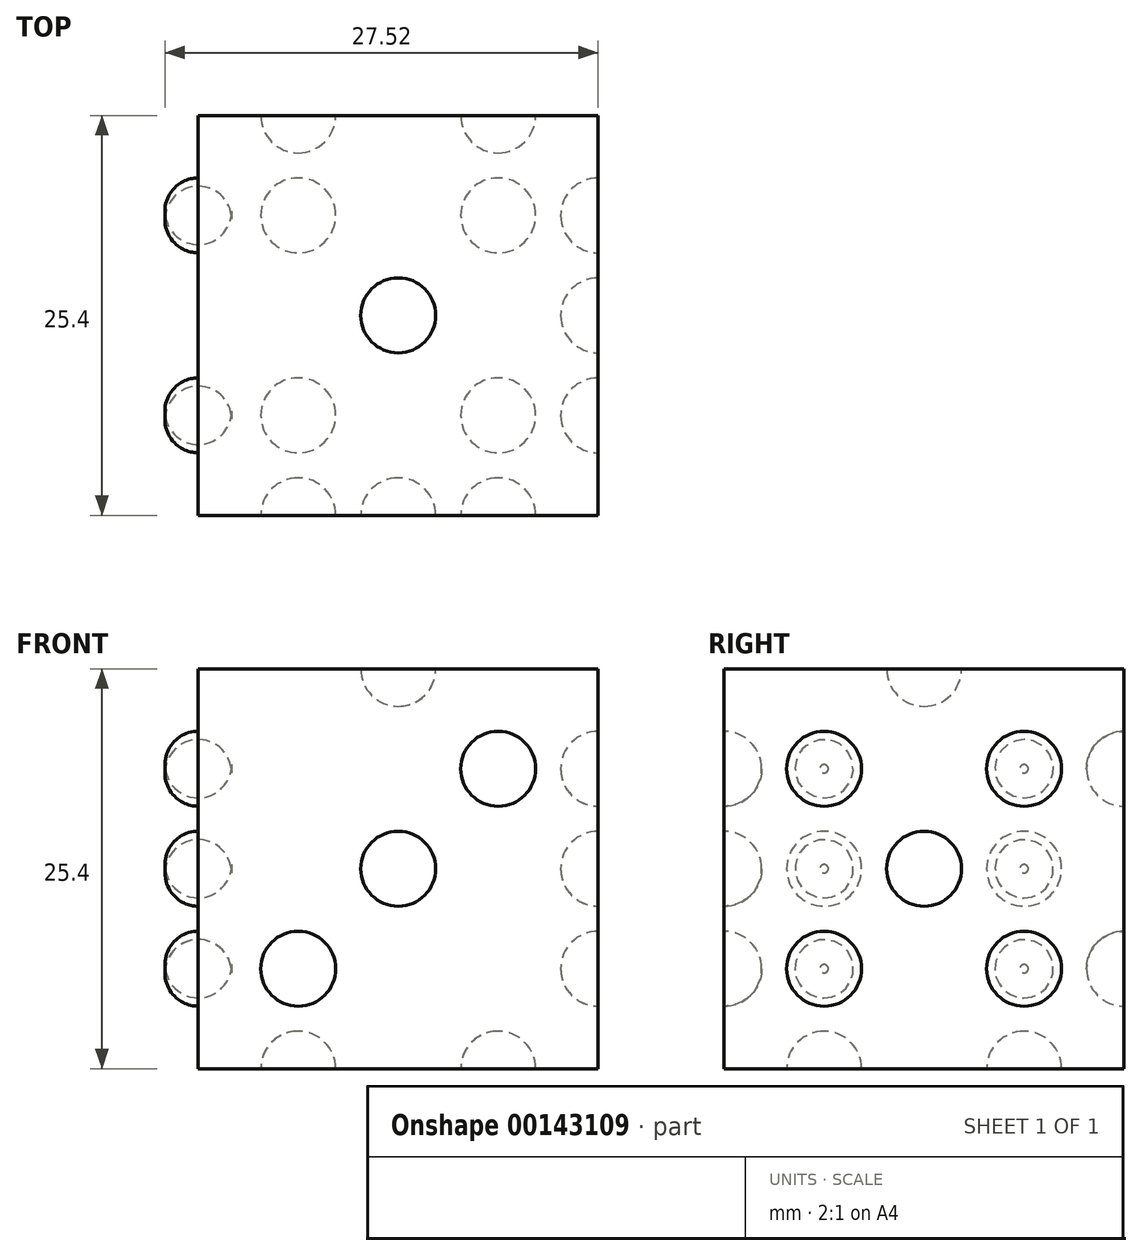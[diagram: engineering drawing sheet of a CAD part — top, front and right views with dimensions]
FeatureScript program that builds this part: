
annotation { "Feature Type Name" : "Feature", "Feature Type Description" : "" }
export const myFeature = defineFeature(function(context is Context, id is Id, definition is map)
    precondition{}
    {
        {
            var Q0;
            Q0=qCreatedBy(makeId("Front.planeOp"),FACE);
            var sketch = newSketch(context, id + "F0", { "sketchPlane" : qUnion([Q0])});
            skLineSegment(sketch, "E0.bottom", {"start": v(0, 0) * mm, "end": v(25.4, 0) * mm});
            skLineSegment(sketch, "E0.top", {"start": v(0, 25.4) * mm, "end": v(25.4, 25.4) * mm});
            skLineSegment(sketch, "E0.left", {"start": v(0, 0) * mm, "end": v(0, 25.4) * mm});
            skLineSegment(sketch, "E0.right", {"start": v(25.4, 0) * mm, "end": v(25.4, 25.4) * mm});
            skSolve(sketch);
        }
        {
            var Q0;
            Q0=makeQuery(id+"F0.imprint","IMPRINT",FACE,{"disambiguationData":[TD([[makeQuery(id+"F0.imprint","IMPRINT",EDGE,{"derivedFrom":sQuery(id+"F0.wireOp",EDGE,"E0.bottom")}),1.0]])]});
            extrude(context, id + "F1", {"entities" : qUnion([Q0]), "oppositeDirection" : true, "depth" : 25.4 * mm});
        }
        {
            var Q0;
            Q0=makeQuery(id+"F1.opExtrude","CAP_FACE",FACE,{"disambiguationData":[OSD([sQuery(id+"F0.wireOp",EDGE,"E0.bottom"),sQuery(id+"F0.wireOp",EDGE,"E0.top"),sQuery(id+"F0.wireOp",EDGE,"E0.left"),sQuery(id+"F0.wireOp",EDGE,"E0.right")])],"isStart":true});
            var sketch = newSketch(context, id + "F2", { "sketchPlane" : qUnion([Q0])});
            skCircle(sketch, "E1", {"center": v(6.35, 6.35) * mm, "radius": 2.38 * mm});
            skCircle(sketch, "E2", {"center": v(12.7, 12.7) * mm, "radius": 2.38 * mm});
            skCircle(sketch, "E3", {"center": v(19.05, 19.05) * mm, "radius": 2.38 * mm});
            skSolve(sketch);
        }
        {
            var Q0;
            Q0=makeQuery(id+"F2.imprint","IMPRINT",FACE,{"disambiguationData":[TD([[makeQuery(id+"F2.imprint","IMPRINT",EDGE,{"derivedFrom":sQuery(id+"F2.wireOp",EDGE,"E1")}),1.0]])]});
            var Q1;
            Q1=makeQuery(id+"F2.imprint","IMPRINT",FACE,{"disambiguationData":[TD([[makeQuery(id+"F2.imprint","IMPRINT",EDGE,{"derivedFrom":sQuery(id+"F2.wireOp",EDGE,"E2")}),1.0]])]});
            var Q2;
            Q2=makeQuery(id+"F2.imprint","IMPRINT",FACE,{"disambiguationData":[TD([[makeQuery(id+"F2.imprint","IMPRINT",EDGE,{"derivedFrom":sQuery(id+"F2.wireOp",EDGE,"E3")}),1.0]])]});
            extrude(context, id + "F3", {"entities" : qUnion([Q0, Q1, Q2]), "operationType" : NewBodyOperationType.REMOVE, "oppositeDirection" : true, "depth" : 2.38 * mm});
        }
        {
            var Q0;
            Q0=makeQuery(id+"F3.boolean.opBoolean","COPY",FACE,{"derivedFrom":makeQuery(id+"F3.opExtrude","CAP_FACE",FACE,{"disambiguationData":[OSD([sQuery(id+"F2.wireOp",EDGE,"E3")])],"isStart":false})});
            var Q1;
            Q1=makeQuery(id+"F3.boolean.opBoolean","COPY",FACE,{"derivedFrom":makeQuery(id+"F3.opExtrude","CAP_FACE",FACE,{"disambiguationData":[OSD([sQuery(id+"F2.wireOp",EDGE,"E2")])],"isStart":false})});
            var Q2;
            Q2=makeQuery(id+"F3.boolean.opBoolean","COPY",FACE,{"derivedFrom":makeQuery(id+"F3.opExtrude","CAP_FACE",FACE,{"disambiguationData":[OSD([sQuery(id+"F2.wireOp",EDGE,"E1")])],"isStart":false})});
            fillet(context, id + "F4", {"entities" : qUnion([Q0, Q1, Q2]), "radius" : 2.38 * mm, "tangentPropagation" : true, "allowEdgeOverflow" : false});
        }
        {
            var Q0;
            Q0=makeQuery(id+"F1.opExtrude","SWEPT_FACE",FACE,{"disambiguationData":[OSD([sQuery(id+"F0.wireOp",EDGE,"E0.right")])]});
            var sketch = newSketch(context, id + "F5", { "sketchPlane" : qUnion([Q0])});
            skCircle(sketch, "E4", {"center": v(12.7, 12.7) * mm, "radius": 2.38 * mm});
            skCircle(sketch, "E5", {"center": v(6.35, 19.05) * mm, "radius": 2.38 * mm});
            skCircle(sketch, "E6", {"center": v(6.35, 6.35) * mm, "radius": 2.38 * mm});
            skCircle(sketch, "E7.MirrorC", {"center": v(19.05, 19.05) * mm, "radius": 2.38 * mm});
            skCircle(sketch, "E8.MirrorC", {"center": v(19.05, 6.35) * mm, "radius": 2.38 * mm});
            skSolve(sketch);
        }
        {
            var Q0;
            Q0 = qSketchRegion(id + "F5", true);
            extrude(context, id + "F6", {"entities" : qUnion([Q0]), "operationType" : NewBodyOperationType.REMOVE, "oppositeDirection" : true, "depth" : 2.38 * mm});
        }
        {
            var Q0;
            Q0=makeQuery(id+"F6.boolean.opBoolean","COPY",FACE,{"derivedFrom":makeQuery(id+"F6.opExtrude","CAP_FACE",FACE,{"disambiguationData":[OSD([sQuery(id+"F5.wireOp",EDGE,"E5")])],"isStart":false})});
            var Q1;
            Q1=makeQuery(id+"F6.boolean.opBoolean","COPY",FACE,{"derivedFrom":makeQuery(id+"F6.opExtrude","CAP_FACE",FACE,{"disambiguationData":[OSD([sQuery(id+"F5.wireOp",EDGE,"E8.MirrorC")])],"isStart":false})});
            var Q2;
            Q2=makeQuery(id+"F6.boolean.opBoolean","COPY",FACE,{"derivedFrom":makeQuery(id+"F6.opExtrude","CAP_FACE",FACE,{"disambiguationData":[OSD([sQuery(id+"F5.wireOp",EDGE,"E7.MirrorC")])],"isStart":false})});
            var Q3;
            Q3=makeQuery(id+"F6.boolean.opBoolean","COPY",FACE,{"derivedFrom":makeQuery(id+"F6.opExtrude","CAP_FACE",FACE,{"disambiguationData":[OSD([sQuery(id+"F5.wireOp",EDGE,"E4")])],"isStart":false})});
            var Q4;
            Q4=makeQuery(id+"F6.boolean.opBoolean","COPY",FACE,{"derivedFrom":makeQuery(id+"F6.opExtrude","CAP_FACE",FACE,{"disambiguationData":[OSD([sQuery(id+"F5.wireOp",EDGE,"E6")])],"isStart":false})});
            fillet(context, id + "F7", {"entities" : qUnion([Q0, Q1, Q2, Q3, Q4]), "radius" : 2.38 * mm, "tangentPropagation" : true, "allowEdgeOverflow" : false});
        }
        {
            var Q0;
            Q0=makeQuery(id+"F1.opExtrude","SWEPT_FACE",FACE,{"disambiguationData":[OSD([sQuery(id+"F0.wireOp",EDGE,"E0.top")])]});
            var sketch = newSketch(context, id + "F8", { "sketchPlane" : qUnion([Q0])});
            skCircle(sketch, "E9", {"center": v(12.7, 12.7) * mm, "radius": 2.38 * mm});
            skSolve(sketch);
        }
        {
            var Q0;
            Q0=makeQuery(id+"F8.imprint","IMPRINT",FACE,{"disambiguationData":[TD([[makeQuery(id+"F8.imprint","IMPRINT",EDGE,{"derivedFrom":sQuery(id+"F8.wireOp",EDGE,"E9")}),1.0]])]});
            extrude(context, id + "F9", {"entities" : qUnion([Q0]), "operationType" : NewBodyOperationType.REMOVE, "oppositeDirection" : true, "depth" : 2.38 * mm});
        }
        {
            var Q0;
            Q0=makeQuery(id+"F9.boolean.opBoolean","COPY",FACE,{"derivedFrom":makeQuery(id+"F9.opExtrude","CAP_FACE",FACE,{"disambiguationData":[OSD([sQuery(id+"F8.wireOp",EDGE,"E9")])],"isStart":false})});
            fillet(context, id + "F10", {"entities" : qUnion([Q0]), "radius" : 2.38 * mm, "tangentPropagation" : true, "allowEdgeOverflow" : false});
        }
        {
            var Q0;
            Q0=makeQuery(id+"F1.opExtrude","SWEPT_FACE",FACE,{"disambiguationData":[OSD([sQuery(id+"F0.wireOp",EDGE,"E0.bottom")])]});
            var sketch = newSketch(context, id + "F11", { "sketchPlane" : qUnion([Q0])});
            skCircle(sketch, "E10", {"center": v(6.35, -6.35) * mm, "radius": 2.38 * mm});
            skCircle(sketch, "E11", {"center": v(6.35, -19.05) * mm, "radius": 2.38 * mm});
            skCircle(sketch, "E12.MirrorC", {"center": v(19.05, -6.35) * mm, "radius": 2.38 * mm});
            skCircle(sketch, "E13.MirrorC", {"center": v(19.05, -19.05) * mm, "radius": 2.38 * mm});
            skSolve(sketch);
        }
        {
            var Q0;
            Q0 = qSketchRegion(id + "F11", true);
            extrude(context, id + "F12", {"entities" : qUnion([Q0]), "operationType" : NewBodyOperationType.REMOVE, "oppositeDirection" : true, "depth" : 2.38 * mm});
        }
        {
            var Q0;
            Q0=makeQuery(id+"F12.boolean.opBoolean","COPY",FACE,{"derivedFrom":makeQuery(id+"F12.opExtrude","CAP_FACE",FACE,{"disambiguationData":[OSD([sQuery(id+"F11.wireOp",EDGE,"E10")])],"isStart":false})});
            var Q1;
            Q1=makeQuery(id+"F12.boolean.opBoolean","COPY",FACE,{"derivedFrom":makeQuery(id+"F12.opExtrude","CAP_FACE",FACE,{"disambiguationData":[OSD([sQuery(id+"F11.wireOp",EDGE,"E12.MirrorC")])],"isStart":false})});
            var Q2;
            Q2=makeQuery(id+"F12.boolean.opBoolean","COPY",FACE,{"derivedFrom":makeQuery(id+"F12.opExtrude","CAP_FACE",FACE,{"disambiguationData":[OSD([sQuery(id+"F11.wireOp",EDGE,"E13.MirrorC")])],"isStart":false})});
            var Q3;
            Q3=makeQuery(id+"F12.boolean.opBoolean","COPY",FACE,{"derivedFrom":makeQuery(id+"F12.opExtrude","CAP_FACE",FACE,{"disambiguationData":[OSD([sQuery(id+"F11.wireOp",EDGE,"E11")])],"isStart":false})});
            fillet(context, id + "F13", {"entities" : qUnion([Q0, Q1, Q2, Q3]), "radius" : 2.38 * mm, "tangentPropagation" : true, "allowEdgeOverflow" : false});
        }
        {
            var Q0;
            Q0=makeQuery(id+"F1.opExtrude","CAP_FACE",FACE,{"disambiguationData":[OSD([sQuery(id+"F0.wireOp",EDGE,"E0.bottom"),sQuery(id+"F0.wireOp",EDGE,"E0.top"),sQuery(id+"F0.wireOp",EDGE,"E0.left"),sQuery(id+"F0.wireOp",EDGE,"E0.right")])],"isStart":false});
            var sketch = newSketch(context, id + "F14", { "sketchPlane" : qUnion([Q0])});
            skCircle(sketch, "E14", {"center": v(-19.05, 19.05) * mm, "radius": 2.38 * mm});
            skCircle(sketch, "E15", {"center": v(-6.35, 6.35) * mm, "radius": 2.38 * mm});
            skSolve(sketch);
        }
        {
            var Q0;
            Q0 = qSketchRegion(id + "F14", true);
            extrude(context, id + "F15", {"entities" : qUnion([Q0]), "operationType" : NewBodyOperationType.REMOVE, "oppositeDirection" : true, "depth" : 2.38 * mm});
        }
        {
            var Q0;
            Q0=makeQuery(id+"F15.boolean.opBoolean","COPY",FACE,{"derivedFrom":makeQuery(id+"F15.opExtrude","CAP_FACE",FACE,{"disambiguationData":[OSD([sQuery(id+"F14.wireOp",EDGE,"E14")])],"isStart":false})});
            var Q1;
            Q1=makeQuery(id+"F15.boolean.opBoolean","COPY",FACE,{"derivedFrom":makeQuery(id+"F15.opExtrude","CAP_FACE",FACE,{"disambiguationData":[OSD([sQuery(id+"F14.wireOp",EDGE,"E15")])],"isStart":false})});
            fillet(context, id + "F16", {"entities" : qUnion([Q0, Q1]), "radius" : 2.38 * mm, "tangentPropagation" : true, "allowEdgeOverflow" : false});
        }
        {
            var Q0;
            Q0=makeQuery(id+"F1.opExtrude","SWEPT_FACE",FACE,{"disambiguationData":[OSD([sQuery(id+"F0.wireOp",EDGE,"E0.left")])]});
            var sketch = newSketch(context, id + "F17", { "sketchPlane" : qUnion([Q0])});
            skCircle(sketch, "E16", {"center": v(-19.05, 19.05) * mm, "radius": 2.38 * mm});
            skCircle(sketch, "E17", {"center": v(-19.05, 6.35) * mm, "radius": 2.38 * mm});
            skCircle(sketch, "E18", {"center": v(-19.05, 12.7) * mm, "radius": 2.38 * mm});
            skCircle(sketch, "E19.MirrorC", {"center": v(-6.35, 19.05) * mm, "radius": 2.38 * mm});
            skCircle(sketch, "E20.MirrorC", {"center": v(-6.35, 12.7) * mm, "radius": 2.38 * mm});
            skCircle(sketch, "E21.MirrorC", {"center": v(-6.35, 6.35) * mm, "radius": 2.38 * mm});
            skSolve(sketch);
        }
        {
            var Q0;
            Q0 = qSketchRegion(id + "F17", true);
            extrude(context, id + "F18", {"entities" : qUnion([Q0]), "operationType" : NewBodyOperationType.REMOVE, "oppositeDirection" : true, "depth" : 2.12 * mm});
        }
        {
            var Q0;
            Q0=makeQuery(id+"F18.boolean.opBoolean","COPY",FACE,{"derivedFrom":makeQuery(id+"F18.opExtrude","CAP_FACE",FACE,{"disambiguationData":[OSD([sQuery(id+"F17.wireOp",EDGE,"E16")])],"isStart":false})});
            var Q1;
            Q1=makeQuery(id+"F18.boolean.opBoolean","COPY",FACE,{"derivedFrom":makeQuery(id+"F18.opExtrude","CAP_FACE",FACE,{"disambiguationData":[OSD([sQuery(id+"F17.wireOp",EDGE,"E18")])],"isStart":false})});
            var Q2;
            Q2=makeQuery(id+"F18.boolean.opBoolean","COPY",FACE,{"derivedFrom":makeQuery(id+"F18.opExtrude","CAP_FACE",FACE,{"disambiguationData":[OSD([sQuery(id+"F17.wireOp",EDGE,"E17")])],"isStart":false})});
            var Q3;
            Q3=makeQuery(id+"F18.boolean.opBoolean","COPY",FACE,{"derivedFrom":makeQuery(id+"F18.opExtrude","CAP_FACE",FACE,{"disambiguationData":[OSD([sQuery(id+"F17.wireOp",EDGE,"E19.MirrorC")])],"isStart":false})});
            var Q4;
            Q4=makeQuery(id+"F18.boolean.opBoolean","COPY",FACE,{"derivedFrom":makeQuery(id+"F18.opExtrude","CAP_FACE",FACE,{"disambiguationData":[OSD([sQuery(id+"F17.wireOp",EDGE,"E20.MirrorC")])],"isStart":false})});
            var Q5;
            Q5=makeQuery(id+"F18.boolean.opBoolean","COPY",FACE,{"derivedFrom":makeQuery(id+"F18.opExtrude","CAP_FACE",FACE,{"disambiguationData":[OSD([sQuery(id+"F17.wireOp",EDGE,"E21.MirrorC")])],"isStart":false})});
            fillet(context, id + "F19", {"entities" : qUnion([Q0, Q1, Q2, Q3, Q4, Q5]), "radius" : 2.12 * mm, "tangentPropagation" : true, "allowEdgeOverflow" : false});
        }
    });
